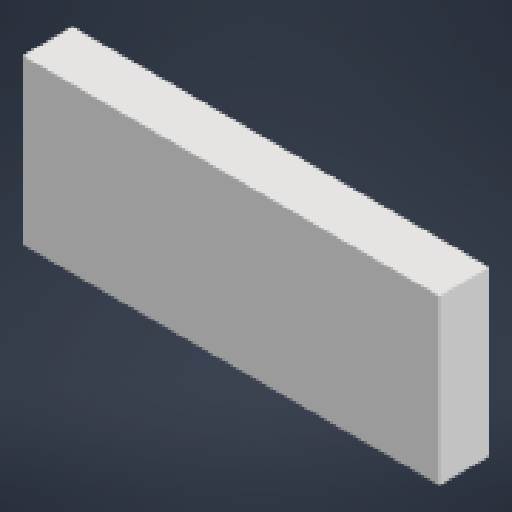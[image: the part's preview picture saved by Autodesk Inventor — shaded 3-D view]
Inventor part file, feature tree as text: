
AUTODESK INVENTOR PART (.ipt)
format: ipt  version: 2025.2 (Build 292293000, 293)  size: 101,888 bytes
history: native  units: in
note: dims shown in document units (in); Inventor stores cm internally (conversion verified against a paired STEP export)
features: other x3, reference x2, extrude x1, sketch x1
ambient origin geometry x8: Origin, YZ Plane, XZ Plane, XY Plane, X Axis, Y Axis, Z Axis, Center Point
bodies: Solid1 (feature_tree)
feature tree (7):
  extrude  "Extrusion1"  [1 undecoded]
  sketch  "Sketch1"  dims[d0=0.7874in d1=0.0in]
  reference  "Reference1"
  reference  "Reference2"
  other  "18650ASSEMBLYfordrawing.iam"
  other  "PILLARSCELLCASE18650:1"
  other  "PILLARSCELLCASE18650:2"
note: 1 required parameter value undecoded (feature->parameter linkage not recoverable at this tier; creation-order binding heuristic only, values carry confidence <= 0.55)
